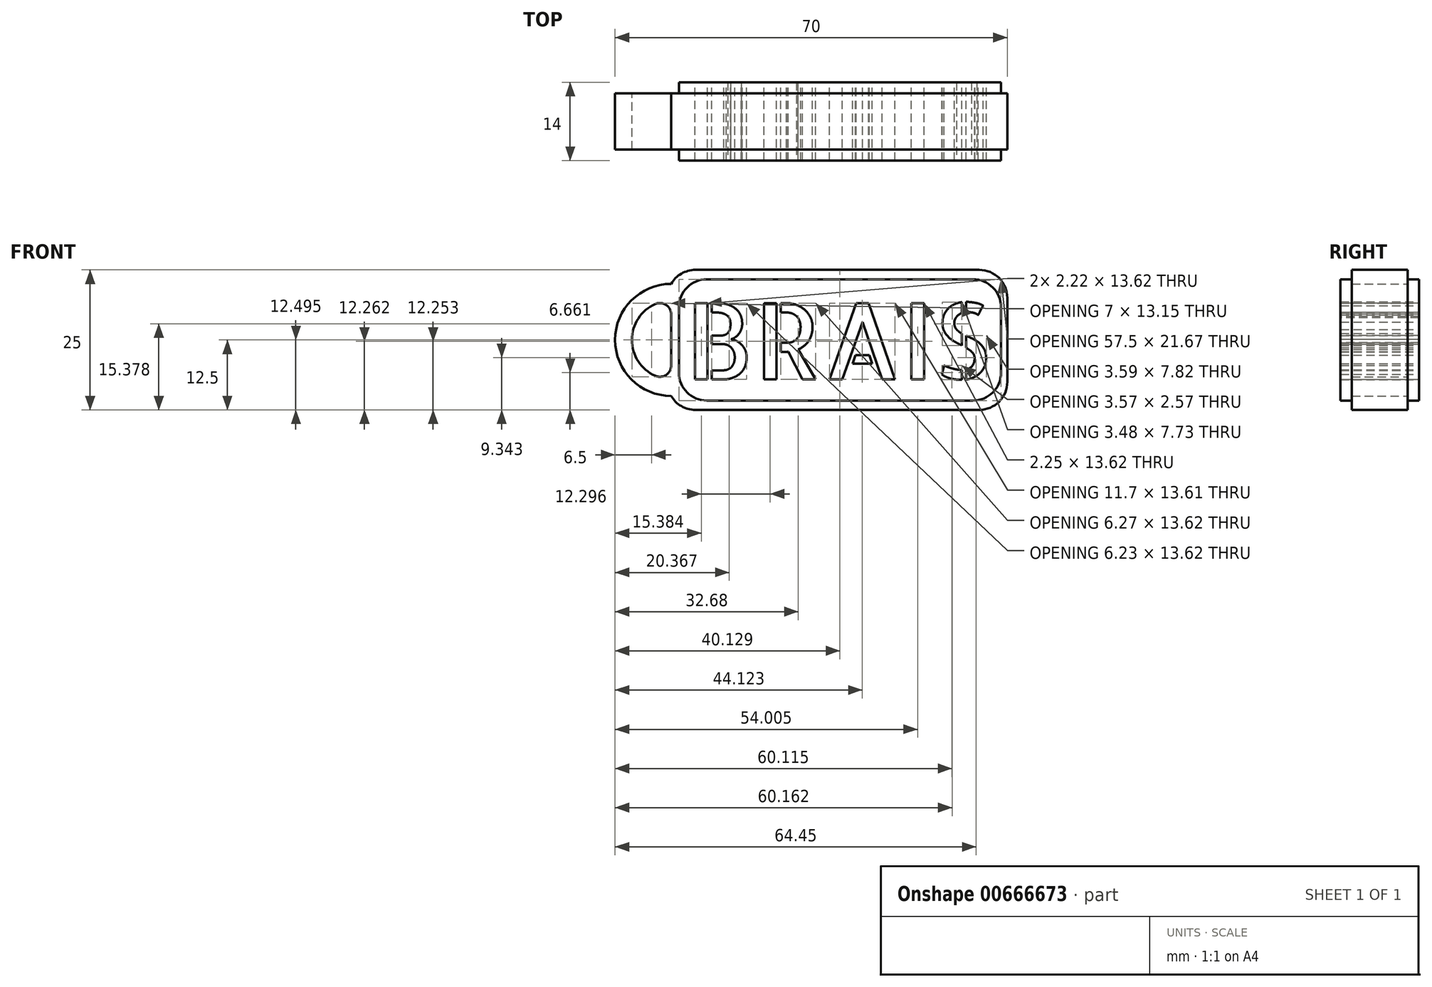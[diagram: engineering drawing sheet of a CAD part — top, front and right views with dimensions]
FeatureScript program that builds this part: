
annotation { "Feature Type Name" : "Feature", "Feature Type Description" : "" }
export const myFeature = defineFeature(function(context is Context, id is Id, definition is map)
    precondition{}
    {
        {
            var Q0;
            Q0=qCreatedBy(makeId("Front.planeOp"),FACE);
            var sketch = newSketch(context, id + "F0", { "sketchPlane" : qUnion([Q0])});
            skLineSegment(sketch, "E0.bottom", {"start": v(-30, 12.5) * mm, "end": v(30, 12.5) * mm});
            skLineSegment(sketch, "E0.top", {"start": v(-30, -12.5) * mm, "end": v(30, -12.5) * mm});
            skLineSegment(sketch, "E0.left", {"start": v(-30, 12.5) * mm, "end": v(-30, -12.5) * mm});
            skLineSegment(sketch, "E0.right", {"start": v(30, 12.5) * mm, "end": v(30, -12.5) * mm});
            skPoint(sketch, "E0.middle", {"position": v(0, 0) * mm});
            skArc(sketch, "E1", {"start": v(-30, 10) * mm, "mid": v(-40, 0) * mm, "end": v(-30, -10) * mm});
            skArc(sketch, "E2", {"start": v(-30, 7) * mm, "mid": v(-37, 0) * mm, "end": v(-30, -7) * mm});
            skText(sketch, "E3", { "text": "BRAIS", "fontName": "AllertaStencil-Regular.ttf"});
            skLineSegment(sketch, "E4.bottom", {"start": v(-28.62, 10.83) * mm, "end": v(28.88, 10.83) * mm});
            skLineSegment(sketch, "E4.top", {"start": v(-28.62, -10.84) * mm, "end": v(28.88, -10.84) * mm});
            skLineSegment(sketch, "E4.left", {"start": v(-28.62, 10.83) * mm, "end": v(-28.62, -10.84) * mm});
            skLineSegment(sketch, "E4.right", {"start": v(28.88, 10.83) * mm, "end": v(28.88, -10.84) * mm});
            const initialGuessF0  = {"E3": [-0.0275, -0.00705, 1, 0, 0.01363]};
            skSetInitialGuess(sketch, initialGuessF0);
            skSolve(sketch);
        }
        {
            var Q0;
            Q0 = qSketchRegion(id + "F0", true);
            var Q1;
            Q1=makeQuery(id+"F0.imprint","IMPRINT",FACE,{"disambiguationData":[TD([[makeQuery(id+"F0.imprint","IMPRINT",EDGE,{"derivedFrom":sQuery(id+"F0.wireOp",EDGE,"E3.sketch_text.stroke-0")}),1.0]])]});
            extrude(context, id + "F1", {"entities" : qUnion([Q0, Q1]), "depth" : 5 * mm, "offsetDistance" : 25 * mm, "hasSecondDirection" : true, "secondDirectionOppositeDirection" : true, "secondDirectionDepth" : 5 * mm});
        }
        {
            var Q0;
            Q0=makeQuery(id+"F1.opExtrude","SWEPT_EDGE",EDGE,{"disambiguationData":[OSD([sQuery(id+"F0.wireOp",EDGE,"E0.bottom"),sQuery(id+"F0.wireOp",EDGE,"E0.right")])]});
            var Q1;
            Q1=makeQuery(id+"F1.opExtrude","SWEPT_EDGE",EDGE,{"disambiguationData":[OSD([sQuery(id+"F0.wireOp",EDGE,"E0.top"),sQuery(id+"F0.wireOp",EDGE,"E0.right")])]});
            var Q2;
            Q2=makeQuery(id+"F1.opExtrude","SWEPT_EDGE",EDGE,{"disambiguationData":[OSD([sQuery(id+"F0.wireOp",EDGE,"E0.bottom"),sQuery(id+"F0.wireOp",EDGE,"E0.left")])]});
            var Q3;
            Q3=makeQuery(id+"F1.opExtrude","SWEPT_EDGE",EDGE,{"disambiguationData":[OSD([sQuery(id+"F0.wireOp",EDGE,"E0.top"),sQuery(id+"F0.wireOp",EDGE,"E0.left")])]});
            fillet(context, id + "F2", {"entities" : qUnion([Q0, Q1, Q2, Q3]), "radius" : 5 * mm, "tangentPropagation" : true, "allowEdgeOverflow" : false});
        }
        {
            var Q0;
            {var subQ0=sQuery(id+"F0.wireOp",EDGE,"E2");var subQ1=sQuery(id+"F0.wireOp",EDGE,"E0.left");Q0=makeQuery(id+"F1.opExtrude","SWEPT_EDGE",EDGE,{"disambiguationData":[OSD([subQ1,subQ0]),TDD([makeQuery(id+"F0.imprint","INTERSECT",VERTEX,{"disambiguationData":[OD(1.0)],"derivedFrom":[subQ1,subQ0]})])]});}
            var Q1;
            {var subQ0=sQuery(id+"F0.wireOp",EDGE,"E2");var subQ1=sQuery(id+"F0.wireOp",EDGE,"E0.left");Q1=makeQuery(id+"F1.opExtrude","SWEPT_EDGE",EDGE,{"disambiguationData":[OSD([subQ1,subQ0]),TDD([makeQuery(id+"F0.imprint","INTERSECT",VERTEX,{"disambiguationData":[OD(0.0)],"derivedFrom":[subQ1,subQ0]})])]});}
            fillet(context, id + "F3", {"entities" : qUnion([Q0, Q1]), "radius" : 2 * mm, "tangentPropagation" : true, "allowEdgeOverflow" : false});
        }
        {
            var Q0;
            Q0=makeQuery(id+"F0.imprint","IMPRINT",FACE,{"disambiguationData":[TD([[makeQuery(id+"F0.imprint","IMPRINT",EDGE,{"derivedFrom":sQuery(id+"F0.wireOp",EDGE,"E3.sketch_text.stroke-0")}),1.0]])]});
            extrude(context, id + "F4", {"entities" : qUnion([Q0]), "operationType" : NewBodyOperationType.ADD, "depth" : 7 * mm, "offsetDistance" : 25 * mm, "hasSecondDirection" : true, "secondDirectionOppositeDirection" : true, "secondDirectionDepth" : 7 * mm});
        }
        {
            var Q0;
            {var subQ0=sQuery(id+"F0.wireOp",EDGE,"E3.sketch_text.stroke-137");var subQ1=sQuery(id+"F0.wireOp",EDGE,"E3.sketch_text.stroke-136");var subQ2=sQuery(id+"F0.wireOp",EDGE,"E3.sketch_text.stroke-135");var subQ3=sQuery(id+"F0.wireOp",EDGE,"E3.sketch_text.stroke-134");var subQ4=sQuery(id+"F0.wireOp",EDGE,"E3.sketch_text.stroke-133");var subQ5=sQuery(id+"F0.wireOp",EDGE,"E3.sketch_text.stroke-132");var subQ6=sQuery(id+"F0.wireOp",EDGE,"E3.sketch_text.stroke-131");var subQ7=sQuery(id+"F0.wireOp",EDGE,"E3.sketch_text.stroke-130");var subQ8=sQuery(id+"F0.wireOp",EDGE,"E3.sketch_text.stroke-129");var subQ9=sQuery(id+"F0.wireOp",EDGE,"E3.sketch_text.stroke-128");var subQ10=sQuery(id+"F0.wireOp",EDGE,"E3.sketch_text.stroke-127");var subQ11=sQuery(id+"F0.wireOp",EDGE,"E3.sketch_text.stroke-126");var subQ12=sQuery(id+"F0.wireOp",EDGE,"E3.sketch_text.stroke-125");var subQ13=sQuery(id+"F0.wireOp",EDGE,"E3.sketch_text.stroke-124");var subQ14=sQuery(id+"F0.wireOp",EDGE,"E3.sketch_text.stroke-123");var subQ15=sQuery(id+"F0.wireOp",EDGE,"E3.sketch_text.stroke-122");var subQ16=sQuery(id+"F0.wireOp",EDGE,"E3.sketch_text.stroke-121");var subQ17=sQuery(id+"F0.wireOp",EDGE,"E3.sketch_text.stroke-120");var subQ18=sQuery(id+"F0.wireOp",EDGE,"E3.sketch_text.stroke-119");var subQ19=sQuery(id+"F0.wireOp",EDGE,"E3.sketch_text.stroke-118");var subQ20=sQuery(id+"F0.wireOp",EDGE,"E3.sketch_text.stroke-117");var subQ21=sQuery(id+"F0.wireOp",EDGE,"E3.sketch_text.stroke-116");var subQ22=sQuery(id+"F0.wireOp",EDGE,"E3.sketch_text.stroke-115");var subQ23=sQuery(id+"F0.wireOp",EDGE,"E3.sketch_text.stroke-114");var subQ24=sQuery(id+"F0.wireOp",EDGE,"E3.sketch_text.stroke-113");var subQ25=sQuery(id+"F0.wireOp",EDGE,"E3.sketch_text.stroke-112");var subQ26=sQuery(id+"F0.wireOp",EDGE,"E3.sketch_text.stroke-111");var subQ27=sQuery(id+"F0.wireOp",EDGE,"E3.sketch_text.stroke-110");var subQ28=sQuery(id+"F0.wireOp",EDGE,"E3.sketch_text.stroke-109");var subQ29=sQuery(id+"F0.wireOp",EDGE,"E3.sketch_text.stroke-108");var subQ30=sQuery(id+"F0.wireOp",EDGE,"E3.sketch_text.stroke-107");var subQ31=sQuery(id+"F0.wireOp",EDGE,"E3.sketch_text.stroke-106");var subQ32=sQuery(id+"F0.wireOp",EDGE,"E3.sketch_text.stroke-105");var subQ33=sQuery(id+"F0.wireOp",EDGE,"E3.sketch_text.stroke-104");var subQ34=sQuery(id+"F0.wireOp",EDGE,"E3.sketch_text.stroke-103");var subQ35=sQuery(id+"F0.wireOp",EDGE,"E3.sketch_text.stroke-102");var subQ36=sQuery(id+"F0.wireOp",EDGE,"E3.sketch_text.stroke-101");var subQ37=sQuery(id+"F0.wireOp",EDGE,"E3.sketch_text.stroke-100");var subQ38=sQuery(id+"F0.wireOp",EDGE,"E3.sketch_text.stroke-99");var subQ39=sQuery(id+"F0.wireOp",EDGE,"E3.sketch_text.stroke-98");var subQ40=sQuery(id+"F0.wireOp",EDGE,"E3.sketch_text.stroke-97");var subQ41=sQuery(id+"F0.wireOp",EDGE,"E3.sketch_text.stroke-96");var subQ42=sQuery(id+"F0.wireOp",EDGE,"E3.sketch_text.stroke-95");var subQ43=sQuery(id+"F0.wireOp",EDGE,"E3.sketch_text.stroke-94");var subQ44=sQuery(id+"F0.wireOp",EDGE,"E3.sketch_text.stroke-93");var subQ45=sQuery(id+"F0.wireOp",EDGE,"E3.sketch_text.stroke-92");var subQ46=sQuery(id+"F0.wireOp",EDGE,"E3.sketch_text.stroke-91");var subQ47=sQuery(id+"F0.wireOp",EDGE,"E3.sketch_text.stroke-90");var subQ48=sQuery(id+"F0.wireOp",EDGE,"E3.sketch_text.stroke-89");var subQ49=sQuery(id+"F0.wireOp",EDGE,"E3.sketch_text.stroke-88");var subQ50=sQuery(id+"F0.wireOp",EDGE,"E3.sketch_text.stroke-87");var subQ51=sQuery(id+"F0.wireOp",EDGE,"E3.sketch_text.stroke-86");var subQ52=sQuery(id+"F0.wireOp",EDGE,"E3.sketch_text.stroke-85");var subQ53=sQuery(id+"F0.wireOp",EDGE,"E3.sketch_text.stroke-84");var subQ54=sQuery(id+"F0.wireOp",EDGE,"E3.sketch_text.stroke-83");var subQ55=sQuery(id+"F0.wireOp",EDGE,"E3.sketch_text.stroke-82");var subQ56=sQuery(id+"F0.wireOp",EDGE,"E3.sketch_text.stroke-81");var subQ57=sQuery(id+"F0.wireOp",EDGE,"E3.sketch_text.stroke-80");var subQ58=sQuery(id+"F0.wireOp",EDGE,"E3.sketch_text.stroke-79");var subQ59=sQuery(id+"F0.wireOp",EDGE,"E3.sketch_text.stroke-78");var subQ60=sQuery(id+"F0.wireOp",EDGE,"E3.sketch_text.stroke-77");var subQ61=sQuery(id+"F0.wireOp",EDGE,"E3.sketch_text.stroke-76");var subQ62=sQuery(id+"F0.wireOp",EDGE,"E3.sketch_text.stroke-75");var subQ63=sQuery(id+"F0.wireOp",EDGE,"E3.sketch_text.stroke-74");var subQ64=sQuery(id+"F0.wireOp",EDGE,"E3.sketch_text.stroke-73");var subQ65=sQuery(id+"F0.wireOp",EDGE,"E3.sketch_text.stroke-72");var subQ66=sQuery(id+"F0.wireOp",EDGE,"E3.sketch_text.stroke-71");var subQ67=sQuery(id+"F0.wireOp",EDGE,"E3.sketch_text.stroke-70");var subQ68=sQuery(id+"F0.wireOp",EDGE,"E3.sketch_text.stroke-69");var subQ69=sQuery(id+"F0.wireOp",EDGE,"E3.sketch_text.stroke-68");var subQ70=sQuery(id+"F0.wireOp",EDGE,"E3.sketch_text.stroke-67");var subQ71=sQuery(id+"F0.wireOp",EDGE,"E3.sketch_text.stroke-66");var subQ72=sQuery(id+"F0.wireOp",EDGE,"E3.sketch_text.stroke-65");var subQ73=sQuery(id+"F0.wireOp",EDGE,"E3.sketch_text.stroke-64");var subQ74=sQuery(id+"F0.wireOp",EDGE,"E3.sketch_text.stroke-63");var subQ75=sQuery(id+"F0.wireOp",EDGE,"E3.sketch_text.stroke-62");var subQ76=sQuery(id+"F0.wireOp",EDGE,"E3.sketch_text.stroke-61");var subQ77=sQuery(id+"F0.wireOp",EDGE,"E3.sketch_text.stroke-60");var subQ78=sQuery(id+"F0.wireOp",EDGE,"E3.sketch_text.stroke-59");var subQ79=sQuery(id+"F0.wireOp",EDGE,"E3.sketch_text.stroke-58");var subQ80=sQuery(id+"F0.wireOp",EDGE,"E3.sketch_text.stroke-57");var subQ81=sQuery(id+"F0.wireOp",EDGE,"E3.sketch_text.stroke-56");var subQ82=sQuery(id+"F0.wireOp",EDGE,"E3.sketch_text.stroke-55");var subQ83=sQuery(id+"F0.wireOp",EDGE,"E3.sketch_text.stroke-54");var subQ84=sQuery(id+"F0.wireOp",EDGE,"E3.sketch_text.stroke-53");var subQ85=sQuery(id+"F0.wireOp",EDGE,"E3.sketch_text.stroke-52");var subQ86=sQuery(id+"F0.wireOp",EDGE,"E3.sketch_text.stroke-51");var subQ87=sQuery(id+"F0.wireOp",EDGE,"E3.sketch_text.stroke-50");var subQ88=sQuery(id+"F0.wireOp",EDGE,"E3.sketch_text.stroke-49");var subQ89=sQuery(id+"F0.wireOp",EDGE,"E3.sketch_text.stroke-48");var subQ90=sQuery(id+"F0.wireOp",EDGE,"E3.sketch_text.stroke-47");var subQ91=sQuery(id+"F0.wireOp",EDGE,"E3.sketch_text.stroke-46");var subQ92=sQuery(id+"F0.wireOp",EDGE,"E3.sketch_text.stroke-45");var subQ93=sQuery(id+"F0.wireOp",EDGE,"E3.sketch_text.stroke-44");var subQ94=sQuery(id+"F0.wireOp",EDGE,"E3.sketch_text.stroke-43");var subQ95=sQuery(id+"F0.wireOp",EDGE,"E3.sketch_text.stroke-42");var subQ96=sQuery(id+"F0.wireOp",EDGE,"E3.sketch_text.stroke-41");var subQ97=sQuery(id+"F0.wireOp",EDGE,"E3.sketch_text.stroke-40");var subQ98=sQuery(id+"F0.wireOp",EDGE,"E3.sketch_text.stroke-39");var subQ99=sQuery(id+"F0.wireOp",EDGE,"E3.sketch_text.stroke-38");var subQ100=sQuery(id+"F0.wireOp",EDGE,"E3.sketch_text.stroke-37");var subQ101=sQuery(id+"F0.wireOp",EDGE,"E3.sketch_text.stroke-36");var subQ102=sQuery(id+"F0.wireOp",EDGE,"E3.sketch_text.stroke-35");var subQ103=sQuery(id+"F0.wireOp",EDGE,"E3.sketch_text.stroke-34");var subQ104=sQuery(id+"F0.wireOp",EDGE,"E3.sketch_text.stroke-33");var subQ105=sQuery(id+"F0.wireOp",EDGE,"E3.sketch_text.stroke-32");var subQ106=sQuery(id+"F0.wireOp",EDGE,"E3.sketch_text.stroke-31");var subQ107=sQuery(id+"F0.wireOp",EDGE,"E3.sketch_text.stroke-30");var subQ108=sQuery(id+"F0.wireOp",EDGE,"E3.sketch_text.stroke-29");var subQ109=sQuery(id+"F0.wireOp",EDGE,"E3.sketch_text.stroke-28");var subQ110=sQuery(id+"F0.wireOp",EDGE,"E3.sketch_text.stroke-27");var subQ111=sQuery(id+"F0.wireOp",EDGE,"E3.sketch_text.stroke-26");var subQ112=sQuery(id+"F0.wireOp",EDGE,"E3.sketch_text.stroke-25");var subQ113=sQuery(id+"F0.wireOp",EDGE,"E3.sketch_text.stroke-24");var subQ114=sQuery(id+"F0.wireOp",EDGE,"E3.sketch_text.stroke-23");var subQ115=sQuery(id+"F0.wireOp",EDGE,"E3.sketch_text.stroke-22");var subQ116=sQuery(id+"F0.wireOp",EDGE,"E3.sketch_text.stroke-21");var subQ117=sQuery(id+"F0.wireOp",EDGE,"E3.sketch_text.stroke-20");var subQ118=sQuery(id+"F0.wireOp",EDGE,"E3.sketch_text.stroke-19");var subQ119=sQuery(id+"F0.wireOp",EDGE,"E3.sketch_text.stroke-18");var subQ120=sQuery(id+"F0.wireOp",EDGE,"E3.sketch_text.stroke-17");var subQ121=sQuery(id+"F0.wireOp",EDGE,"E3.sketch_text.stroke-16");var subQ122=sQuery(id+"F0.wireOp",EDGE,"E3.sketch_text.stroke-15");var subQ123=sQuery(id+"F0.wireOp",EDGE,"E3.sketch_text.stroke-14");var subQ124=sQuery(id+"F0.wireOp",EDGE,"E3.sketch_text.stroke-13");var subQ125=sQuery(id+"F0.wireOp",EDGE,"E3.sketch_text.stroke-12");var subQ126=sQuery(id+"F0.wireOp",EDGE,"E3.sketch_text.stroke-11");var subQ127=sQuery(id+"F0.wireOp",EDGE,"E3.sketch_text.stroke-10");var subQ128=sQuery(id+"F0.wireOp",EDGE,"E3.sketch_text.stroke-9");var subQ129=sQuery(id+"F0.wireOp",EDGE,"E3.sketch_text.stroke-8");var subQ130=sQuery(id+"F0.wireOp",EDGE,"E3.sketch_text.stroke-7");var subQ131=sQuery(id+"F0.wireOp",EDGE,"E3.sketch_text.stroke-6");var subQ132=sQuery(id+"F0.wireOp",EDGE,"E3.sketch_text.stroke-5");var subQ133=sQuery(id+"F0.wireOp",EDGE,"E3.sketch_text.stroke-4");var subQ134=sQuery(id+"F0.wireOp",EDGE,"E3.sketch_text.stroke-3");var subQ135=sQuery(id+"F0.wireOp",EDGE,"E3.sketch_text.stroke-2");var subQ136=sQuery(id+"F0.wireOp",EDGE,"E3.sketch_text.stroke-1");var subQ137=sQuery(id+"F0.wireOp",EDGE,"E3.sketch_text.stroke-0");var subQ138=sQuery(id+"F0.wireOp",EDGE,"E4.left");var subQ139=sQuery(id+"F0.wireOp",EDGE,"E4.bottom");Q0=makeQuery(id+"F4.boolean.opBoolean","SPLIT",EDGE,{"disambiguationData":[TD([makeQuery(id+"F4.opExtrude","CAP_FACE",FACE,{"disambiguationData":[OSD([subQ137,subQ136,subQ135,subQ134,subQ133,subQ132,subQ131,subQ130,subQ129,subQ128,subQ127,subQ126,subQ125,subQ124,subQ123,subQ122,subQ121,subQ120,subQ119,subQ118,subQ117,subQ116,subQ115,subQ114,subQ113,subQ112,subQ111,subQ110,subQ109,subQ108,subQ107,subQ106,subQ105,subQ104,subQ103,subQ102,subQ101,subQ100,subQ99,subQ98,subQ97,subQ96,subQ95,subQ94,subQ93,subQ92,subQ91,subQ90,subQ89,subQ88,subQ87,subQ86,subQ85,subQ84,subQ83,subQ82,subQ81,subQ80,subQ79,subQ78,subQ77,subQ76,subQ75,subQ74,subQ73,subQ72,subQ71,subQ70,subQ69,subQ68,subQ67,subQ66,subQ65,subQ64,subQ63,subQ62,subQ61,subQ60,subQ59,subQ58,subQ57,subQ56,subQ55,subQ54,subQ53,subQ52,subQ51,subQ50,subQ49,subQ48,subQ47,subQ46,subQ45,subQ44,subQ43,subQ42,subQ41,subQ40,subQ39,subQ38,subQ37,subQ36,subQ35,subQ34,subQ33,subQ32,subQ31,subQ30,subQ29,subQ28,subQ27,subQ26,subQ25,subQ24,subQ23,subQ22,subQ21,subQ20,subQ19,subQ18,subQ17,subQ16,subQ15,subQ14,subQ13,subQ12,subQ11,subQ10,subQ9,subQ8,subQ7,subQ6,subQ5,subQ4,subQ3,subQ2,subQ1,subQ0,subQ139,sQuery(id+"F0.wireOp",EDGE,"E4.top"),subQ138,sQuery(id+"F0.wireOp",EDGE,"E4.right")])],"isStart":false})])],"derivedFrom":makeQuery(id+"F4.opExtrude","SWEPT_EDGE",EDGE,{"disambiguationData":[OSD([subQ139,subQ138])]})});}
            var Q1;
            {var subQ0=sQuery(id+"F0.wireOp",EDGE,"E3.sketch_text.stroke-137");var subQ1=sQuery(id+"F0.wireOp",EDGE,"E3.sketch_text.stroke-136");var subQ2=sQuery(id+"F0.wireOp",EDGE,"E3.sketch_text.stroke-135");var subQ3=sQuery(id+"F0.wireOp",EDGE,"E3.sketch_text.stroke-134");var subQ4=sQuery(id+"F0.wireOp",EDGE,"E3.sketch_text.stroke-133");var subQ5=sQuery(id+"F0.wireOp",EDGE,"E3.sketch_text.stroke-132");var subQ6=sQuery(id+"F0.wireOp",EDGE,"E3.sketch_text.stroke-131");var subQ7=sQuery(id+"F0.wireOp",EDGE,"E3.sketch_text.stroke-130");var subQ8=sQuery(id+"F0.wireOp",EDGE,"E3.sketch_text.stroke-129");var subQ9=sQuery(id+"F0.wireOp",EDGE,"E3.sketch_text.stroke-128");var subQ10=sQuery(id+"F0.wireOp",EDGE,"E3.sketch_text.stroke-127");var subQ11=sQuery(id+"F0.wireOp",EDGE,"E3.sketch_text.stroke-126");var subQ12=sQuery(id+"F0.wireOp",EDGE,"E3.sketch_text.stroke-125");var subQ13=sQuery(id+"F0.wireOp",EDGE,"E3.sketch_text.stroke-124");var subQ14=sQuery(id+"F0.wireOp",EDGE,"E3.sketch_text.stroke-123");var subQ15=sQuery(id+"F0.wireOp",EDGE,"E3.sketch_text.stroke-122");var subQ16=sQuery(id+"F0.wireOp",EDGE,"E3.sketch_text.stroke-121");var subQ17=sQuery(id+"F0.wireOp",EDGE,"E3.sketch_text.stroke-120");var subQ18=sQuery(id+"F0.wireOp",EDGE,"E3.sketch_text.stroke-119");var subQ19=sQuery(id+"F0.wireOp",EDGE,"E3.sketch_text.stroke-118");var subQ20=sQuery(id+"F0.wireOp",EDGE,"E3.sketch_text.stroke-117");var subQ21=sQuery(id+"F0.wireOp",EDGE,"E3.sketch_text.stroke-116");var subQ22=sQuery(id+"F0.wireOp",EDGE,"E3.sketch_text.stroke-115");var subQ23=sQuery(id+"F0.wireOp",EDGE,"E3.sketch_text.stroke-114");var subQ24=sQuery(id+"F0.wireOp",EDGE,"E3.sketch_text.stroke-113");var subQ25=sQuery(id+"F0.wireOp",EDGE,"E3.sketch_text.stroke-112");var subQ26=sQuery(id+"F0.wireOp",EDGE,"E3.sketch_text.stroke-111");var subQ27=sQuery(id+"F0.wireOp",EDGE,"E3.sketch_text.stroke-110");var subQ28=sQuery(id+"F0.wireOp",EDGE,"E3.sketch_text.stroke-109");var subQ29=sQuery(id+"F0.wireOp",EDGE,"E3.sketch_text.stroke-108");var subQ30=sQuery(id+"F0.wireOp",EDGE,"E3.sketch_text.stroke-107");var subQ31=sQuery(id+"F0.wireOp",EDGE,"E3.sketch_text.stroke-106");var subQ32=sQuery(id+"F0.wireOp",EDGE,"E3.sketch_text.stroke-105");var subQ33=sQuery(id+"F0.wireOp",EDGE,"E3.sketch_text.stroke-104");var subQ34=sQuery(id+"F0.wireOp",EDGE,"E3.sketch_text.stroke-103");var subQ35=sQuery(id+"F0.wireOp",EDGE,"E3.sketch_text.stroke-102");var subQ36=sQuery(id+"F0.wireOp",EDGE,"E3.sketch_text.stroke-101");var subQ37=sQuery(id+"F0.wireOp",EDGE,"E3.sketch_text.stroke-100");var subQ38=sQuery(id+"F0.wireOp",EDGE,"E3.sketch_text.stroke-99");var subQ39=sQuery(id+"F0.wireOp",EDGE,"E3.sketch_text.stroke-98");var subQ40=sQuery(id+"F0.wireOp",EDGE,"E3.sketch_text.stroke-97");var subQ41=sQuery(id+"F0.wireOp",EDGE,"E3.sketch_text.stroke-96");var subQ42=sQuery(id+"F0.wireOp",EDGE,"E3.sketch_text.stroke-95");var subQ43=sQuery(id+"F0.wireOp",EDGE,"E3.sketch_text.stroke-94");var subQ44=sQuery(id+"F0.wireOp",EDGE,"E3.sketch_text.stroke-93");var subQ45=sQuery(id+"F0.wireOp",EDGE,"E3.sketch_text.stroke-92");var subQ46=sQuery(id+"F0.wireOp",EDGE,"E3.sketch_text.stroke-91");var subQ47=sQuery(id+"F0.wireOp",EDGE,"E3.sketch_text.stroke-90");var subQ48=sQuery(id+"F0.wireOp",EDGE,"E3.sketch_text.stroke-89");var subQ49=sQuery(id+"F0.wireOp",EDGE,"E3.sketch_text.stroke-88");var subQ50=sQuery(id+"F0.wireOp",EDGE,"E3.sketch_text.stroke-87");var subQ51=sQuery(id+"F0.wireOp",EDGE,"E3.sketch_text.stroke-86");var subQ52=sQuery(id+"F0.wireOp",EDGE,"E3.sketch_text.stroke-85");var subQ53=sQuery(id+"F0.wireOp",EDGE,"E3.sketch_text.stroke-84");var subQ54=sQuery(id+"F0.wireOp",EDGE,"E3.sketch_text.stroke-83");var subQ55=sQuery(id+"F0.wireOp",EDGE,"E3.sketch_text.stroke-82");var subQ56=sQuery(id+"F0.wireOp",EDGE,"E3.sketch_text.stroke-81");var subQ57=sQuery(id+"F0.wireOp",EDGE,"E3.sketch_text.stroke-80");var subQ58=sQuery(id+"F0.wireOp",EDGE,"E3.sketch_text.stroke-79");var subQ59=sQuery(id+"F0.wireOp",EDGE,"E3.sketch_text.stroke-78");var subQ60=sQuery(id+"F0.wireOp",EDGE,"E3.sketch_text.stroke-77");var subQ61=sQuery(id+"F0.wireOp",EDGE,"E3.sketch_text.stroke-76");var subQ62=sQuery(id+"F0.wireOp",EDGE,"E3.sketch_text.stroke-75");var subQ63=sQuery(id+"F0.wireOp",EDGE,"E3.sketch_text.stroke-74");var subQ64=sQuery(id+"F0.wireOp",EDGE,"E3.sketch_text.stroke-73");var subQ65=sQuery(id+"F0.wireOp",EDGE,"E3.sketch_text.stroke-72");var subQ66=sQuery(id+"F0.wireOp",EDGE,"E3.sketch_text.stroke-71");var subQ67=sQuery(id+"F0.wireOp",EDGE,"E3.sketch_text.stroke-70");var subQ68=sQuery(id+"F0.wireOp",EDGE,"E3.sketch_text.stroke-69");var subQ69=sQuery(id+"F0.wireOp",EDGE,"E3.sketch_text.stroke-68");var subQ70=sQuery(id+"F0.wireOp",EDGE,"E3.sketch_text.stroke-67");var subQ71=sQuery(id+"F0.wireOp",EDGE,"E3.sketch_text.stroke-66");var subQ72=sQuery(id+"F0.wireOp",EDGE,"E3.sketch_text.stroke-65");var subQ73=sQuery(id+"F0.wireOp",EDGE,"E3.sketch_text.stroke-64");var subQ74=sQuery(id+"F0.wireOp",EDGE,"E3.sketch_text.stroke-63");var subQ75=sQuery(id+"F0.wireOp",EDGE,"E3.sketch_text.stroke-62");var subQ76=sQuery(id+"F0.wireOp",EDGE,"E3.sketch_text.stroke-61");var subQ77=sQuery(id+"F0.wireOp",EDGE,"E3.sketch_text.stroke-60");var subQ78=sQuery(id+"F0.wireOp",EDGE,"E3.sketch_text.stroke-59");var subQ79=sQuery(id+"F0.wireOp",EDGE,"E3.sketch_text.stroke-58");var subQ80=sQuery(id+"F0.wireOp",EDGE,"E3.sketch_text.stroke-57");var subQ81=sQuery(id+"F0.wireOp",EDGE,"E3.sketch_text.stroke-56");var subQ82=sQuery(id+"F0.wireOp",EDGE,"E3.sketch_text.stroke-55");var subQ83=sQuery(id+"F0.wireOp",EDGE,"E3.sketch_text.stroke-54");var subQ84=sQuery(id+"F0.wireOp",EDGE,"E3.sketch_text.stroke-53");var subQ85=sQuery(id+"F0.wireOp",EDGE,"E3.sketch_text.stroke-52");var subQ86=sQuery(id+"F0.wireOp",EDGE,"E3.sketch_text.stroke-51");var subQ87=sQuery(id+"F0.wireOp",EDGE,"E3.sketch_text.stroke-50");var subQ88=sQuery(id+"F0.wireOp",EDGE,"E3.sketch_text.stroke-49");var subQ89=sQuery(id+"F0.wireOp",EDGE,"E3.sketch_text.stroke-48");var subQ90=sQuery(id+"F0.wireOp",EDGE,"E3.sketch_text.stroke-47");var subQ91=sQuery(id+"F0.wireOp",EDGE,"E3.sketch_text.stroke-46");var subQ92=sQuery(id+"F0.wireOp",EDGE,"E3.sketch_text.stroke-45");var subQ93=sQuery(id+"F0.wireOp",EDGE,"E3.sketch_text.stroke-44");var subQ94=sQuery(id+"F0.wireOp",EDGE,"E3.sketch_text.stroke-43");var subQ95=sQuery(id+"F0.wireOp",EDGE,"E3.sketch_text.stroke-42");var subQ96=sQuery(id+"F0.wireOp",EDGE,"E3.sketch_text.stroke-41");var subQ97=sQuery(id+"F0.wireOp",EDGE,"E3.sketch_text.stroke-40");var subQ98=sQuery(id+"F0.wireOp",EDGE,"E3.sketch_text.stroke-39");var subQ99=sQuery(id+"F0.wireOp",EDGE,"E3.sketch_text.stroke-38");var subQ100=sQuery(id+"F0.wireOp",EDGE,"E3.sketch_text.stroke-37");var subQ101=sQuery(id+"F0.wireOp",EDGE,"E3.sketch_text.stroke-36");var subQ102=sQuery(id+"F0.wireOp",EDGE,"E3.sketch_text.stroke-35");var subQ103=sQuery(id+"F0.wireOp",EDGE,"E3.sketch_text.stroke-34");var subQ104=sQuery(id+"F0.wireOp",EDGE,"E3.sketch_text.stroke-33");var subQ105=sQuery(id+"F0.wireOp",EDGE,"E3.sketch_text.stroke-32");var subQ106=sQuery(id+"F0.wireOp",EDGE,"E3.sketch_text.stroke-31");var subQ107=sQuery(id+"F0.wireOp",EDGE,"E3.sketch_text.stroke-30");var subQ108=sQuery(id+"F0.wireOp",EDGE,"E3.sketch_text.stroke-29");var subQ109=sQuery(id+"F0.wireOp",EDGE,"E3.sketch_text.stroke-28");var subQ110=sQuery(id+"F0.wireOp",EDGE,"E3.sketch_text.stroke-27");var subQ111=sQuery(id+"F0.wireOp",EDGE,"E3.sketch_text.stroke-26");var subQ112=sQuery(id+"F0.wireOp",EDGE,"E3.sketch_text.stroke-25");var subQ113=sQuery(id+"F0.wireOp",EDGE,"E3.sketch_text.stroke-24");var subQ114=sQuery(id+"F0.wireOp",EDGE,"E3.sketch_text.stroke-23");var subQ115=sQuery(id+"F0.wireOp",EDGE,"E3.sketch_text.stroke-22");var subQ116=sQuery(id+"F0.wireOp",EDGE,"E3.sketch_text.stroke-21");var subQ117=sQuery(id+"F0.wireOp",EDGE,"E3.sketch_text.stroke-20");var subQ118=sQuery(id+"F0.wireOp",EDGE,"E3.sketch_text.stroke-19");var subQ119=sQuery(id+"F0.wireOp",EDGE,"E3.sketch_text.stroke-18");var subQ120=sQuery(id+"F0.wireOp",EDGE,"E3.sketch_text.stroke-17");var subQ121=sQuery(id+"F0.wireOp",EDGE,"E3.sketch_text.stroke-16");var subQ122=sQuery(id+"F0.wireOp",EDGE,"E3.sketch_text.stroke-15");var subQ123=sQuery(id+"F0.wireOp",EDGE,"E3.sketch_text.stroke-14");var subQ124=sQuery(id+"F0.wireOp",EDGE,"E3.sketch_text.stroke-13");var subQ125=sQuery(id+"F0.wireOp",EDGE,"E3.sketch_text.stroke-12");var subQ126=sQuery(id+"F0.wireOp",EDGE,"E3.sketch_text.stroke-11");var subQ127=sQuery(id+"F0.wireOp",EDGE,"E3.sketch_text.stroke-10");var subQ128=sQuery(id+"F0.wireOp",EDGE,"E3.sketch_text.stroke-9");var subQ129=sQuery(id+"F0.wireOp",EDGE,"E3.sketch_text.stroke-8");var subQ130=sQuery(id+"F0.wireOp",EDGE,"E3.sketch_text.stroke-7");var subQ131=sQuery(id+"F0.wireOp",EDGE,"E3.sketch_text.stroke-6");var subQ132=sQuery(id+"F0.wireOp",EDGE,"E3.sketch_text.stroke-5");var subQ133=sQuery(id+"F0.wireOp",EDGE,"E3.sketch_text.stroke-4");var subQ134=sQuery(id+"F0.wireOp",EDGE,"E3.sketch_text.stroke-3");var subQ135=sQuery(id+"F0.wireOp",EDGE,"E3.sketch_text.stroke-2");var subQ136=sQuery(id+"F0.wireOp",EDGE,"E3.sketch_text.stroke-1");var subQ137=sQuery(id+"F0.wireOp",EDGE,"E3.sketch_text.stroke-0");var subQ138=sQuery(id+"F0.wireOp",EDGE,"E4.left");var subQ139=sQuery(id+"F0.wireOp",EDGE,"E4.top");Q1=makeQuery(id+"F4.boolean.opBoolean","SPLIT",EDGE,{"disambiguationData":[TD([makeQuery(id+"F4.opExtrude","CAP_FACE",FACE,{"disambiguationData":[OSD([subQ137,subQ136,subQ135,subQ134,subQ133,subQ132,subQ131,subQ130,subQ129,subQ128,subQ127,subQ126,subQ125,subQ124,subQ123,subQ122,subQ121,subQ120,subQ119,subQ118,subQ117,subQ116,subQ115,subQ114,subQ113,subQ112,subQ111,subQ110,subQ109,subQ108,subQ107,subQ106,subQ105,subQ104,subQ103,subQ102,subQ101,subQ100,subQ99,subQ98,subQ97,subQ96,subQ95,subQ94,subQ93,subQ92,subQ91,subQ90,subQ89,subQ88,subQ87,subQ86,subQ85,subQ84,subQ83,subQ82,subQ81,subQ80,subQ79,subQ78,subQ77,subQ76,subQ75,subQ74,subQ73,subQ72,subQ71,subQ70,subQ69,subQ68,subQ67,subQ66,subQ65,subQ64,subQ63,subQ62,subQ61,subQ60,subQ59,subQ58,subQ57,subQ56,subQ55,subQ54,subQ53,subQ52,subQ51,subQ50,subQ49,subQ48,subQ47,subQ46,subQ45,subQ44,subQ43,subQ42,subQ41,subQ40,subQ39,subQ38,subQ37,subQ36,subQ35,subQ34,subQ33,subQ32,subQ31,subQ30,subQ29,subQ28,subQ27,subQ26,subQ25,subQ24,subQ23,subQ22,subQ21,subQ20,subQ19,subQ18,subQ17,subQ16,subQ15,subQ14,subQ13,subQ12,subQ11,subQ10,subQ9,subQ8,subQ7,subQ6,subQ5,subQ4,subQ3,subQ2,subQ1,subQ0,sQuery(id+"F0.wireOp",EDGE,"E4.bottom"),subQ139,subQ138,sQuery(id+"F0.wireOp",EDGE,"E4.right")])],"isStart":false})])],"derivedFrom":makeQuery(id+"F4.opExtrude","SWEPT_EDGE",EDGE,{"disambiguationData":[OSD([subQ139,subQ138])]})});}
            var Q2;
            Q2=makeQuery(id+"F4.opExtrude","SWEPT_EDGE",EDGE,{"disambiguationData":[OSD([sQuery(id+"F0.wireOp",EDGE,"E4.top"),sQuery(id+"F0.wireOp",EDGE,"E4.right")])]});
            var Q3;
            Q3=makeQuery(id+"F4.opExtrude","SWEPT_EDGE",EDGE,{"disambiguationData":[OSD([sQuery(id+"F0.wireOp",EDGE,"E4.bottom"),sQuery(id+"F0.wireOp",EDGE,"E4.right")])]});
            var Q4;
            {var subQ0=sQuery(id+"F0.wireOp",EDGE,"E3.sketch_text.stroke-137");var subQ1=sQuery(id+"F0.wireOp",EDGE,"E3.sketch_text.stroke-136");var subQ2=sQuery(id+"F0.wireOp",EDGE,"E3.sketch_text.stroke-135");var subQ3=sQuery(id+"F0.wireOp",EDGE,"E3.sketch_text.stroke-134");var subQ4=sQuery(id+"F0.wireOp",EDGE,"E3.sketch_text.stroke-133");var subQ5=sQuery(id+"F0.wireOp",EDGE,"E3.sketch_text.stroke-132");var subQ6=sQuery(id+"F0.wireOp",EDGE,"E3.sketch_text.stroke-131");var subQ7=sQuery(id+"F0.wireOp",EDGE,"E3.sketch_text.stroke-130");var subQ8=sQuery(id+"F0.wireOp",EDGE,"E3.sketch_text.stroke-129");var subQ9=sQuery(id+"F0.wireOp",EDGE,"E3.sketch_text.stroke-128");var subQ10=sQuery(id+"F0.wireOp",EDGE,"E3.sketch_text.stroke-127");var subQ11=sQuery(id+"F0.wireOp",EDGE,"E3.sketch_text.stroke-126");var subQ12=sQuery(id+"F0.wireOp",EDGE,"E3.sketch_text.stroke-125");var subQ13=sQuery(id+"F0.wireOp",EDGE,"E3.sketch_text.stroke-124");var subQ14=sQuery(id+"F0.wireOp",EDGE,"E3.sketch_text.stroke-123");var subQ15=sQuery(id+"F0.wireOp",EDGE,"E3.sketch_text.stroke-122");var subQ16=sQuery(id+"F0.wireOp",EDGE,"E3.sketch_text.stroke-121");var subQ17=sQuery(id+"F0.wireOp",EDGE,"E3.sketch_text.stroke-120");var subQ18=sQuery(id+"F0.wireOp",EDGE,"E3.sketch_text.stroke-119");var subQ19=sQuery(id+"F0.wireOp",EDGE,"E3.sketch_text.stroke-118");var subQ20=sQuery(id+"F0.wireOp",EDGE,"E3.sketch_text.stroke-117");var subQ21=sQuery(id+"F0.wireOp",EDGE,"E3.sketch_text.stroke-116");var subQ22=sQuery(id+"F0.wireOp",EDGE,"E3.sketch_text.stroke-115");var subQ23=sQuery(id+"F0.wireOp",EDGE,"E3.sketch_text.stroke-114");var subQ24=sQuery(id+"F0.wireOp",EDGE,"E3.sketch_text.stroke-113");var subQ25=sQuery(id+"F0.wireOp",EDGE,"E3.sketch_text.stroke-112");var subQ26=sQuery(id+"F0.wireOp",EDGE,"E3.sketch_text.stroke-111");var subQ27=sQuery(id+"F0.wireOp",EDGE,"E3.sketch_text.stroke-110");var subQ28=sQuery(id+"F0.wireOp",EDGE,"E3.sketch_text.stroke-109");var subQ29=sQuery(id+"F0.wireOp",EDGE,"E3.sketch_text.stroke-108");var subQ30=sQuery(id+"F0.wireOp",EDGE,"E3.sketch_text.stroke-107");var subQ31=sQuery(id+"F0.wireOp",EDGE,"E3.sketch_text.stroke-106");var subQ32=sQuery(id+"F0.wireOp",EDGE,"E3.sketch_text.stroke-105");var subQ33=sQuery(id+"F0.wireOp",EDGE,"E3.sketch_text.stroke-104");var subQ34=sQuery(id+"F0.wireOp",EDGE,"E3.sketch_text.stroke-103");var subQ35=sQuery(id+"F0.wireOp",EDGE,"E3.sketch_text.stroke-102");var subQ36=sQuery(id+"F0.wireOp",EDGE,"E3.sketch_text.stroke-101");var subQ37=sQuery(id+"F0.wireOp",EDGE,"E3.sketch_text.stroke-100");var subQ38=sQuery(id+"F0.wireOp",EDGE,"E3.sketch_text.stroke-99");var subQ39=sQuery(id+"F0.wireOp",EDGE,"E3.sketch_text.stroke-98");var subQ40=sQuery(id+"F0.wireOp",EDGE,"E3.sketch_text.stroke-97");var subQ41=sQuery(id+"F0.wireOp",EDGE,"E3.sketch_text.stroke-96");var subQ42=sQuery(id+"F0.wireOp",EDGE,"E3.sketch_text.stroke-95");var subQ43=sQuery(id+"F0.wireOp",EDGE,"E3.sketch_text.stroke-94");var subQ44=sQuery(id+"F0.wireOp",EDGE,"E3.sketch_text.stroke-93");var subQ45=sQuery(id+"F0.wireOp",EDGE,"E3.sketch_text.stroke-92");var subQ46=sQuery(id+"F0.wireOp",EDGE,"E3.sketch_text.stroke-91");var subQ47=sQuery(id+"F0.wireOp",EDGE,"E3.sketch_text.stroke-90");var subQ48=sQuery(id+"F0.wireOp",EDGE,"E3.sketch_text.stroke-89");var subQ49=sQuery(id+"F0.wireOp",EDGE,"E3.sketch_text.stroke-88");var subQ50=sQuery(id+"F0.wireOp",EDGE,"E3.sketch_text.stroke-87");var subQ51=sQuery(id+"F0.wireOp",EDGE,"E3.sketch_text.stroke-86");var subQ52=sQuery(id+"F0.wireOp",EDGE,"E3.sketch_text.stroke-85");var subQ53=sQuery(id+"F0.wireOp",EDGE,"E3.sketch_text.stroke-84");var subQ54=sQuery(id+"F0.wireOp",EDGE,"E3.sketch_text.stroke-83");var subQ55=sQuery(id+"F0.wireOp",EDGE,"E3.sketch_text.stroke-82");var subQ56=sQuery(id+"F0.wireOp",EDGE,"E3.sketch_text.stroke-81");var subQ57=sQuery(id+"F0.wireOp",EDGE,"E3.sketch_text.stroke-80");var subQ58=sQuery(id+"F0.wireOp",EDGE,"E3.sketch_text.stroke-79");var subQ59=sQuery(id+"F0.wireOp",EDGE,"E3.sketch_text.stroke-78");var subQ60=sQuery(id+"F0.wireOp",EDGE,"E3.sketch_text.stroke-77");var subQ61=sQuery(id+"F0.wireOp",EDGE,"E3.sketch_text.stroke-76");var subQ62=sQuery(id+"F0.wireOp",EDGE,"E3.sketch_text.stroke-75");var subQ63=sQuery(id+"F0.wireOp",EDGE,"E3.sketch_text.stroke-74");var subQ64=sQuery(id+"F0.wireOp",EDGE,"E3.sketch_text.stroke-73");var subQ65=sQuery(id+"F0.wireOp",EDGE,"E3.sketch_text.stroke-72");var subQ66=sQuery(id+"F0.wireOp",EDGE,"E3.sketch_text.stroke-71");var subQ67=sQuery(id+"F0.wireOp",EDGE,"E3.sketch_text.stroke-70");var subQ68=sQuery(id+"F0.wireOp",EDGE,"E3.sketch_text.stroke-69");var subQ69=sQuery(id+"F0.wireOp",EDGE,"E3.sketch_text.stroke-68");var subQ70=sQuery(id+"F0.wireOp",EDGE,"E3.sketch_text.stroke-67");var subQ71=sQuery(id+"F0.wireOp",EDGE,"E3.sketch_text.stroke-66");var subQ72=sQuery(id+"F0.wireOp",EDGE,"E3.sketch_text.stroke-65");var subQ73=sQuery(id+"F0.wireOp",EDGE,"E3.sketch_text.stroke-64");var subQ74=sQuery(id+"F0.wireOp",EDGE,"E3.sketch_text.stroke-63");var subQ75=sQuery(id+"F0.wireOp",EDGE,"E3.sketch_text.stroke-62");var subQ76=sQuery(id+"F0.wireOp",EDGE,"E3.sketch_text.stroke-61");var subQ77=sQuery(id+"F0.wireOp",EDGE,"E3.sketch_text.stroke-60");var subQ78=sQuery(id+"F0.wireOp",EDGE,"E3.sketch_text.stroke-59");var subQ79=sQuery(id+"F0.wireOp",EDGE,"E3.sketch_text.stroke-58");var subQ80=sQuery(id+"F0.wireOp",EDGE,"E3.sketch_text.stroke-57");var subQ81=sQuery(id+"F0.wireOp",EDGE,"E3.sketch_text.stroke-56");var subQ82=sQuery(id+"F0.wireOp",EDGE,"E3.sketch_text.stroke-55");var subQ83=sQuery(id+"F0.wireOp",EDGE,"E3.sketch_text.stroke-54");var subQ84=sQuery(id+"F0.wireOp",EDGE,"E3.sketch_text.stroke-53");var subQ85=sQuery(id+"F0.wireOp",EDGE,"E3.sketch_text.stroke-52");var subQ86=sQuery(id+"F0.wireOp",EDGE,"E3.sketch_text.stroke-51");var subQ87=sQuery(id+"F0.wireOp",EDGE,"E3.sketch_text.stroke-50");var subQ88=sQuery(id+"F0.wireOp",EDGE,"E3.sketch_text.stroke-49");var subQ89=sQuery(id+"F0.wireOp",EDGE,"E3.sketch_text.stroke-48");var subQ90=sQuery(id+"F0.wireOp",EDGE,"E3.sketch_text.stroke-47");var subQ91=sQuery(id+"F0.wireOp",EDGE,"E3.sketch_text.stroke-46");var subQ92=sQuery(id+"F0.wireOp",EDGE,"E3.sketch_text.stroke-45");var subQ93=sQuery(id+"F0.wireOp",EDGE,"E3.sketch_text.stroke-44");var subQ94=sQuery(id+"F0.wireOp",EDGE,"E3.sketch_text.stroke-43");var subQ95=sQuery(id+"F0.wireOp",EDGE,"E3.sketch_text.stroke-42");var subQ96=sQuery(id+"F0.wireOp",EDGE,"E3.sketch_text.stroke-41");var subQ97=sQuery(id+"F0.wireOp",EDGE,"E3.sketch_text.stroke-40");var subQ98=sQuery(id+"F0.wireOp",EDGE,"E3.sketch_text.stroke-39");var subQ99=sQuery(id+"F0.wireOp",EDGE,"E3.sketch_text.stroke-38");var subQ100=sQuery(id+"F0.wireOp",EDGE,"E3.sketch_text.stroke-37");var subQ101=sQuery(id+"F0.wireOp",EDGE,"E3.sketch_text.stroke-36");var subQ102=sQuery(id+"F0.wireOp",EDGE,"E3.sketch_text.stroke-35");var subQ103=sQuery(id+"F0.wireOp",EDGE,"E3.sketch_text.stroke-34");var subQ104=sQuery(id+"F0.wireOp",EDGE,"E3.sketch_text.stroke-33");var subQ105=sQuery(id+"F0.wireOp",EDGE,"E3.sketch_text.stroke-32");var subQ106=sQuery(id+"F0.wireOp",EDGE,"E3.sketch_text.stroke-31");var subQ107=sQuery(id+"F0.wireOp",EDGE,"E3.sketch_text.stroke-30");var subQ108=sQuery(id+"F0.wireOp",EDGE,"E3.sketch_text.stroke-29");var subQ109=sQuery(id+"F0.wireOp",EDGE,"E3.sketch_text.stroke-28");var subQ110=sQuery(id+"F0.wireOp",EDGE,"E3.sketch_text.stroke-27");var subQ111=sQuery(id+"F0.wireOp",EDGE,"E3.sketch_text.stroke-26");var subQ112=sQuery(id+"F0.wireOp",EDGE,"E3.sketch_text.stroke-25");var subQ113=sQuery(id+"F0.wireOp",EDGE,"E3.sketch_text.stroke-24");var subQ114=sQuery(id+"F0.wireOp",EDGE,"E3.sketch_text.stroke-23");var subQ115=sQuery(id+"F0.wireOp",EDGE,"E3.sketch_text.stroke-22");var subQ116=sQuery(id+"F0.wireOp",EDGE,"E3.sketch_text.stroke-21");var subQ117=sQuery(id+"F0.wireOp",EDGE,"E3.sketch_text.stroke-20");var subQ118=sQuery(id+"F0.wireOp",EDGE,"E3.sketch_text.stroke-19");var subQ119=sQuery(id+"F0.wireOp",EDGE,"E3.sketch_text.stroke-18");var subQ120=sQuery(id+"F0.wireOp",EDGE,"E3.sketch_text.stroke-17");var subQ121=sQuery(id+"F0.wireOp",EDGE,"E3.sketch_text.stroke-16");var subQ122=sQuery(id+"F0.wireOp",EDGE,"E3.sketch_text.stroke-15");var subQ123=sQuery(id+"F0.wireOp",EDGE,"E3.sketch_text.stroke-14");var subQ124=sQuery(id+"F0.wireOp",EDGE,"E3.sketch_text.stroke-13");var subQ125=sQuery(id+"F0.wireOp",EDGE,"E3.sketch_text.stroke-12");var subQ126=sQuery(id+"F0.wireOp",EDGE,"E3.sketch_text.stroke-11");var subQ127=sQuery(id+"F0.wireOp",EDGE,"E3.sketch_text.stroke-10");var subQ128=sQuery(id+"F0.wireOp",EDGE,"E3.sketch_text.stroke-9");var subQ129=sQuery(id+"F0.wireOp",EDGE,"E3.sketch_text.stroke-8");var subQ130=sQuery(id+"F0.wireOp",EDGE,"E3.sketch_text.stroke-7");var subQ131=sQuery(id+"F0.wireOp",EDGE,"E3.sketch_text.stroke-6");var subQ132=sQuery(id+"F0.wireOp",EDGE,"E3.sketch_text.stroke-5");var subQ133=sQuery(id+"F0.wireOp",EDGE,"E3.sketch_text.stroke-4");var subQ134=sQuery(id+"F0.wireOp",EDGE,"E3.sketch_text.stroke-3");var subQ135=sQuery(id+"F0.wireOp",EDGE,"E3.sketch_text.stroke-2");var subQ136=sQuery(id+"F0.wireOp",EDGE,"E3.sketch_text.stroke-1");var subQ137=sQuery(id+"F0.wireOp",EDGE,"E3.sketch_text.stroke-0");var subQ138=sQuery(id+"F0.wireOp",EDGE,"E4.left");var subQ139=sQuery(id+"F0.wireOp",EDGE,"E4.bottom");Q4=makeQuery(id+"F4.boolean.opBoolean","SPLIT",EDGE,{"disambiguationData":[TD([makeQuery(id+"F4.opExtrude","CAP_FACE",FACE,{"disambiguationData":[OSD([subQ137,subQ136,subQ135,subQ134,subQ133,subQ132,subQ131,subQ130,subQ129,subQ128,subQ127,subQ126,subQ125,subQ124,subQ123,subQ122,subQ121,subQ120,subQ119,subQ118,subQ117,subQ116,subQ115,subQ114,subQ113,subQ112,subQ111,subQ110,subQ109,subQ108,subQ107,subQ106,subQ105,subQ104,subQ103,subQ102,subQ101,subQ100,subQ99,subQ98,subQ97,subQ96,subQ95,subQ94,subQ93,subQ92,subQ91,subQ90,subQ89,subQ88,subQ87,subQ86,subQ85,subQ84,subQ83,subQ82,subQ81,subQ80,subQ79,subQ78,subQ77,subQ76,subQ75,subQ74,subQ73,subQ72,subQ71,subQ70,subQ69,subQ68,subQ67,subQ66,subQ65,subQ64,subQ63,subQ62,subQ61,subQ60,subQ59,subQ58,subQ57,subQ56,subQ55,subQ54,subQ53,subQ52,subQ51,subQ50,subQ49,subQ48,subQ47,subQ46,subQ45,subQ44,subQ43,subQ42,subQ41,subQ40,subQ39,subQ38,subQ37,subQ36,subQ35,subQ34,subQ33,subQ32,subQ31,subQ30,subQ29,subQ28,subQ27,subQ26,subQ25,subQ24,subQ23,subQ22,subQ21,subQ20,subQ19,subQ18,subQ17,subQ16,subQ15,subQ14,subQ13,subQ12,subQ11,subQ10,subQ9,subQ8,subQ7,subQ6,subQ5,subQ4,subQ3,subQ2,subQ1,subQ0,subQ139,sQuery(id+"F0.wireOp",EDGE,"E4.top"),subQ138,sQuery(id+"F0.wireOp",EDGE,"E4.right")])],"isStart":true})])],"derivedFrom":makeQuery(id+"F4.opExtrude","SWEPT_EDGE",EDGE,{"disambiguationData":[OSD([subQ139,subQ138])]})});}
            var Q5;
            {var subQ0=sQuery(id+"F0.wireOp",EDGE,"E3.sketch_text.stroke-137");var subQ1=sQuery(id+"F0.wireOp",EDGE,"E3.sketch_text.stroke-136");var subQ2=sQuery(id+"F0.wireOp",EDGE,"E3.sketch_text.stroke-135");var subQ3=sQuery(id+"F0.wireOp",EDGE,"E3.sketch_text.stroke-134");var subQ4=sQuery(id+"F0.wireOp",EDGE,"E3.sketch_text.stroke-133");var subQ5=sQuery(id+"F0.wireOp",EDGE,"E3.sketch_text.stroke-132");var subQ6=sQuery(id+"F0.wireOp",EDGE,"E3.sketch_text.stroke-131");var subQ7=sQuery(id+"F0.wireOp",EDGE,"E3.sketch_text.stroke-130");var subQ8=sQuery(id+"F0.wireOp",EDGE,"E3.sketch_text.stroke-129");var subQ9=sQuery(id+"F0.wireOp",EDGE,"E3.sketch_text.stroke-128");var subQ10=sQuery(id+"F0.wireOp",EDGE,"E3.sketch_text.stroke-127");var subQ11=sQuery(id+"F0.wireOp",EDGE,"E3.sketch_text.stroke-126");var subQ12=sQuery(id+"F0.wireOp",EDGE,"E3.sketch_text.stroke-125");var subQ13=sQuery(id+"F0.wireOp",EDGE,"E3.sketch_text.stroke-124");var subQ14=sQuery(id+"F0.wireOp",EDGE,"E3.sketch_text.stroke-123");var subQ15=sQuery(id+"F0.wireOp",EDGE,"E3.sketch_text.stroke-122");var subQ16=sQuery(id+"F0.wireOp",EDGE,"E3.sketch_text.stroke-121");var subQ17=sQuery(id+"F0.wireOp",EDGE,"E3.sketch_text.stroke-120");var subQ18=sQuery(id+"F0.wireOp",EDGE,"E3.sketch_text.stroke-119");var subQ19=sQuery(id+"F0.wireOp",EDGE,"E3.sketch_text.stroke-118");var subQ20=sQuery(id+"F0.wireOp",EDGE,"E3.sketch_text.stroke-117");var subQ21=sQuery(id+"F0.wireOp",EDGE,"E3.sketch_text.stroke-116");var subQ22=sQuery(id+"F0.wireOp",EDGE,"E3.sketch_text.stroke-115");var subQ23=sQuery(id+"F0.wireOp",EDGE,"E3.sketch_text.stroke-114");var subQ24=sQuery(id+"F0.wireOp",EDGE,"E3.sketch_text.stroke-113");var subQ25=sQuery(id+"F0.wireOp",EDGE,"E3.sketch_text.stroke-112");var subQ26=sQuery(id+"F0.wireOp",EDGE,"E3.sketch_text.stroke-111");var subQ27=sQuery(id+"F0.wireOp",EDGE,"E3.sketch_text.stroke-110");var subQ28=sQuery(id+"F0.wireOp",EDGE,"E3.sketch_text.stroke-109");var subQ29=sQuery(id+"F0.wireOp",EDGE,"E3.sketch_text.stroke-108");var subQ30=sQuery(id+"F0.wireOp",EDGE,"E3.sketch_text.stroke-107");var subQ31=sQuery(id+"F0.wireOp",EDGE,"E3.sketch_text.stroke-106");var subQ32=sQuery(id+"F0.wireOp",EDGE,"E3.sketch_text.stroke-105");var subQ33=sQuery(id+"F0.wireOp",EDGE,"E3.sketch_text.stroke-104");var subQ34=sQuery(id+"F0.wireOp",EDGE,"E3.sketch_text.stroke-103");var subQ35=sQuery(id+"F0.wireOp",EDGE,"E3.sketch_text.stroke-102");var subQ36=sQuery(id+"F0.wireOp",EDGE,"E3.sketch_text.stroke-101");var subQ37=sQuery(id+"F0.wireOp",EDGE,"E3.sketch_text.stroke-100");var subQ38=sQuery(id+"F0.wireOp",EDGE,"E3.sketch_text.stroke-99");var subQ39=sQuery(id+"F0.wireOp",EDGE,"E3.sketch_text.stroke-98");var subQ40=sQuery(id+"F0.wireOp",EDGE,"E3.sketch_text.stroke-97");var subQ41=sQuery(id+"F0.wireOp",EDGE,"E3.sketch_text.stroke-96");var subQ42=sQuery(id+"F0.wireOp",EDGE,"E3.sketch_text.stroke-95");var subQ43=sQuery(id+"F0.wireOp",EDGE,"E3.sketch_text.stroke-94");var subQ44=sQuery(id+"F0.wireOp",EDGE,"E3.sketch_text.stroke-93");var subQ45=sQuery(id+"F0.wireOp",EDGE,"E3.sketch_text.stroke-92");var subQ46=sQuery(id+"F0.wireOp",EDGE,"E3.sketch_text.stroke-91");var subQ47=sQuery(id+"F0.wireOp",EDGE,"E3.sketch_text.stroke-90");var subQ48=sQuery(id+"F0.wireOp",EDGE,"E3.sketch_text.stroke-89");var subQ49=sQuery(id+"F0.wireOp",EDGE,"E3.sketch_text.stroke-88");var subQ50=sQuery(id+"F0.wireOp",EDGE,"E3.sketch_text.stroke-87");var subQ51=sQuery(id+"F0.wireOp",EDGE,"E3.sketch_text.stroke-86");var subQ52=sQuery(id+"F0.wireOp",EDGE,"E3.sketch_text.stroke-85");var subQ53=sQuery(id+"F0.wireOp",EDGE,"E3.sketch_text.stroke-84");var subQ54=sQuery(id+"F0.wireOp",EDGE,"E3.sketch_text.stroke-83");var subQ55=sQuery(id+"F0.wireOp",EDGE,"E3.sketch_text.stroke-82");var subQ56=sQuery(id+"F0.wireOp",EDGE,"E3.sketch_text.stroke-81");var subQ57=sQuery(id+"F0.wireOp",EDGE,"E3.sketch_text.stroke-80");var subQ58=sQuery(id+"F0.wireOp",EDGE,"E3.sketch_text.stroke-79");var subQ59=sQuery(id+"F0.wireOp",EDGE,"E3.sketch_text.stroke-78");var subQ60=sQuery(id+"F0.wireOp",EDGE,"E3.sketch_text.stroke-77");var subQ61=sQuery(id+"F0.wireOp",EDGE,"E3.sketch_text.stroke-76");var subQ62=sQuery(id+"F0.wireOp",EDGE,"E3.sketch_text.stroke-75");var subQ63=sQuery(id+"F0.wireOp",EDGE,"E3.sketch_text.stroke-74");var subQ64=sQuery(id+"F0.wireOp",EDGE,"E3.sketch_text.stroke-73");var subQ65=sQuery(id+"F0.wireOp",EDGE,"E3.sketch_text.stroke-72");var subQ66=sQuery(id+"F0.wireOp",EDGE,"E3.sketch_text.stroke-71");var subQ67=sQuery(id+"F0.wireOp",EDGE,"E3.sketch_text.stroke-70");var subQ68=sQuery(id+"F0.wireOp",EDGE,"E3.sketch_text.stroke-69");var subQ69=sQuery(id+"F0.wireOp",EDGE,"E3.sketch_text.stroke-68");var subQ70=sQuery(id+"F0.wireOp",EDGE,"E3.sketch_text.stroke-67");var subQ71=sQuery(id+"F0.wireOp",EDGE,"E3.sketch_text.stroke-66");var subQ72=sQuery(id+"F0.wireOp",EDGE,"E3.sketch_text.stroke-65");var subQ73=sQuery(id+"F0.wireOp",EDGE,"E3.sketch_text.stroke-64");var subQ74=sQuery(id+"F0.wireOp",EDGE,"E3.sketch_text.stroke-63");var subQ75=sQuery(id+"F0.wireOp",EDGE,"E3.sketch_text.stroke-62");var subQ76=sQuery(id+"F0.wireOp",EDGE,"E3.sketch_text.stroke-61");var subQ77=sQuery(id+"F0.wireOp",EDGE,"E3.sketch_text.stroke-60");var subQ78=sQuery(id+"F0.wireOp",EDGE,"E3.sketch_text.stroke-59");var subQ79=sQuery(id+"F0.wireOp",EDGE,"E3.sketch_text.stroke-58");var subQ80=sQuery(id+"F0.wireOp",EDGE,"E3.sketch_text.stroke-57");var subQ81=sQuery(id+"F0.wireOp",EDGE,"E3.sketch_text.stroke-56");var subQ82=sQuery(id+"F0.wireOp",EDGE,"E3.sketch_text.stroke-55");var subQ83=sQuery(id+"F0.wireOp",EDGE,"E3.sketch_text.stroke-54");var subQ84=sQuery(id+"F0.wireOp",EDGE,"E3.sketch_text.stroke-53");var subQ85=sQuery(id+"F0.wireOp",EDGE,"E3.sketch_text.stroke-52");var subQ86=sQuery(id+"F0.wireOp",EDGE,"E3.sketch_text.stroke-51");var subQ87=sQuery(id+"F0.wireOp",EDGE,"E3.sketch_text.stroke-50");var subQ88=sQuery(id+"F0.wireOp",EDGE,"E3.sketch_text.stroke-49");var subQ89=sQuery(id+"F0.wireOp",EDGE,"E3.sketch_text.stroke-48");var subQ90=sQuery(id+"F0.wireOp",EDGE,"E3.sketch_text.stroke-47");var subQ91=sQuery(id+"F0.wireOp",EDGE,"E3.sketch_text.stroke-46");var subQ92=sQuery(id+"F0.wireOp",EDGE,"E3.sketch_text.stroke-45");var subQ93=sQuery(id+"F0.wireOp",EDGE,"E3.sketch_text.stroke-44");var subQ94=sQuery(id+"F0.wireOp",EDGE,"E3.sketch_text.stroke-43");var subQ95=sQuery(id+"F0.wireOp",EDGE,"E3.sketch_text.stroke-42");var subQ96=sQuery(id+"F0.wireOp",EDGE,"E3.sketch_text.stroke-41");var subQ97=sQuery(id+"F0.wireOp",EDGE,"E3.sketch_text.stroke-40");var subQ98=sQuery(id+"F0.wireOp",EDGE,"E3.sketch_text.stroke-39");var subQ99=sQuery(id+"F0.wireOp",EDGE,"E3.sketch_text.stroke-38");var subQ100=sQuery(id+"F0.wireOp",EDGE,"E3.sketch_text.stroke-37");var subQ101=sQuery(id+"F0.wireOp",EDGE,"E3.sketch_text.stroke-36");var subQ102=sQuery(id+"F0.wireOp",EDGE,"E3.sketch_text.stroke-35");var subQ103=sQuery(id+"F0.wireOp",EDGE,"E3.sketch_text.stroke-34");var subQ104=sQuery(id+"F0.wireOp",EDGE,"E3.sketch_text.stroke-33");var subQ105=sQuery(id+"F0.wireOp",EDGE,"E3.sketch_text.stroke-32");var subQ106=sQuery(id+"F0.wireOp",EDGE,"E3.sketch_text.stroke-31");var subQ107=sQuery(id+"F0.wireOp",EDGE,"E3.sketch_text.stroke-30");var subQ108=sQuery(id+"F0.wireOp",EDGE,"E3.sketch_text.stroke-29");var subQ109=sQuery(id+"F0.wireOp",EDGE,"E3.sketch_text.stroke-28");var subQ110=sQuery(id+"F0.wireOp",EDGE,"E3.sketch_text.stroke-27");var subQ111=sQuery(id+"F0.wireOp",EDGE,"E3.sketch_text.stroke-26");var subQ112=sQuery(id+"F0.wireOp",EDGE,"E3.sketch_text.stroke-25");var subQ113=sQuery(id+"F0.wireOp",EDGE,"E3.sketch_text.stroke-24");var subQ114=sQuery(id+"F0.wireOp",EDGE,"E3.sketch_text.stroke-23");var subQ115=sQuery(id+"F0.wireOp",EDGE,"E3.sketch_text.stroke-22");var subQ116=sQuery(id+"F0.wireOp",EDGE,"E3.sketch_text.stroke-21");var subQ117=sQuery(id+"F0.wireOp",EDGE,"E3.sketch_text.stroke-20");var subQ118=sQuery(id+"F0.wireOp",EDGE,"E3.sketch_text.stroke-19");var subQ119=sQuery(id+"F0.wireOp",EDGE,"E3.sketch_text.stroke-18");var subQ120=sQuery(id+"F0.wireOp",EDGE,"E3.sketch_text.stroke-17");var subQ121=sQuery(id+"F0.wireOp",EDGE,"E3.sketch_text.stroke-16");var subQ122=sQuery(id+"F0.wireOp",EDGE,"E3.sketch_text.stroke-15");var subQ123=sQuery(id+"F0.wireOp",EDGE,"E3.sketch_text.stroke-14");var subQ124=sQuery(id+"F0.wireOp",EDGE,"E3.sketch_text.stroke-13");var subQ125=sQuery(id+"F0.wireOp",EDGE,"E3.sketch_text.stroke-12");var subQ126=sQuery(id+"F0.wireOp",EDGE,"E3.sketch_text.stroke-11");var subQ127=sQuery(id+"F0.wireOp",EDGE,"E3.sketch_text.stroke-10");var subQ128=sQuery(id+"F0.wireOp",EDGE,"E3.sketch_text.stroke-9");var subQ129=sQuery(id+"F0.wireOp",EDGE,"E3.sketch_text.stroke-8");var subQ130=sQuery(id+"F0.wireOp",EDGE,"E3.sketch_text.stroke-7");var subQ131=sQuery(id+"F0.wireOp",EDGE,"E3.sketch_text.stroke-6");var subQ132=sQuery(id+"F0.wireOp",EDGE,"E3.sketch_text.stroke-5");var subQ133=sQuery(id+"F0.wireOp",EDGE,"E3.sketch_text.stroke-4");var subQ134=sQuery(id+"F0.wireOp",EDGE,"E3.sketch_text.stroke-3");var subQ135=sQuery(id+"F0.wireOp",EDGE,"E3.sketch_text.stroke-2");var subQ136=sQuery(id+"F0.wireOp",EDGE,"E3.sketch_text.stroke-1");var subQ137=sQuery(id+"F0.wireOp",EDGE,"E3.sketch_text.stroke-0");var subQ138=sQuery(id+"F0.wireOp",EDGE,"E4.left");var subQ139=sQuery(id+"F0.wireOp",EDGE,"E4.top");Q5=makeQuery(id+"F4.boolean.opBoolean","SPLIT",EDGE,{"disambiguationData":[TD([makeQuery(id+"F4.opExtrude","CAP_FACE",FACE,{"disambiguationData":[OSD([subQ137,subQ136,subQ135,subQ134,subQ133,subQ132,subQ131,subQ130,subQ129,subQ128,subQ127,subQ126,subQ125,subQ124,subQ123,subQ122,subQ121,subQ120,subQ119,subQ118,subQ117,subQ116,subQ115,subQ114,subQ113,subQ112,subQ111,subQ110,subQ109,subQ108,subQ107,subQ106,subQ105,subQ104,subQ103,subQ102,subQ101,subQ100,subQ99,subQ98,subQ97,subQ96,subQ95,subQ94,subQ93,subQ92,subQ91,subQ90,subQ89,subQ88,subQ87,subQ86,subQ85,subQ84,subQ83,subQ82,subQ81,subQ80,subQ79,subQ78,subQ77,subQ76,subQ75,subQ74,subQ73,subQ72,subQ71,subQ70,subQ69,subQ68,subQ67,subQ66,subQ65,subQ64,subQ63,subQ62,subQ61,subQ60,subQ59,subQ58,subQ57,subQ56,subQ55,subQ54,subQ53,subQ52,subQ51,subQ50,subQ49,subQ48,subQ47,subQ46,subQ45,subQ44,subQ43,subQ42,subQ41,subQ40,subQ39,subQ38,subQ37,subQ36,subQ35,subQ34,subQ33,subQ32,subQ31,subQ30,subQ29,subQ28,subQ27,subQ26,subQ25,subQ24,subQ23,subQ22,subQ21,subQ20,subQ19,subQ18,subQ17,subQ16,subQ15,subQ14,subQ13,subQ12,subQ11,subQ10,subQ9,subQ8,subQ7,subQ6,subQ5,subQ4,subQ3,subQ2,subQ1,subQ0,sQuery(id+"F0.wireOp",EDGE,"E4.bottom"),subQ139,subQ138,sQuery(id+"F0.wireOp",EDGE,"E4.right")])],"isStart":true})])],"derivedFrom":makeQuery(id+"F4.opExtrude","SWEPT_EDGE",EDGE,{"disambiguationData":[OSD([subQ139,subQ138])]})});}
            fillet(context, id + "F5", {"entities" : qUnion([Q0, Q1, Q2, Q3, Q4, Q5]), "radius" : 5 * mm, "tangentPropagation" : true, "allowEdgeOverflow" : false});
        }
    });
